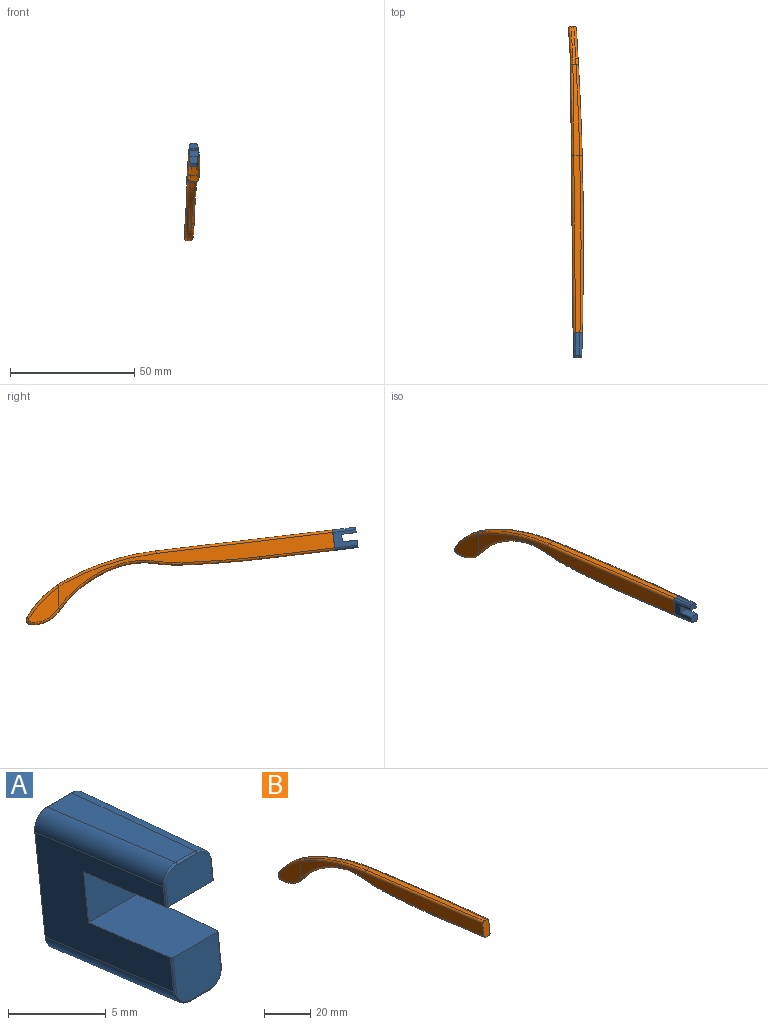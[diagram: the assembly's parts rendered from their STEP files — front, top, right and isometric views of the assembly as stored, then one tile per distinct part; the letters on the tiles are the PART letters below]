
ASSEMBLY  parts=2 mates=1
PART A: 32 faces, bbox 4.2x25.4x61.7 mm
  f0: plane 5.95x3.66mm, normal (0,-0.12,-0.99), area 21.2mm2, adj f1,f3,f11,f12,f27,f31
  f1: plane 3.66x3mm, normal (0,-0.99,0.12), area 11mm2, adj f0,f2,f11,f12
  f2: plane 5.95x3.65mm, normal (0,0.12,0.99), area 21.1mm2, adj f1,f4,f11,f12,f22,f26
  f3: plane 3.23x2.06mm, normal (0,-0.99,0.12), area 6.3mm2, adj f0,f27,f28,f29,f30,f31
  f4: plane 3.34x3.07mm, normal (0,-0.99,0.12), area 9.1mm2, adj f2,f22,f23,f24,f25,f26
  f5: bspline ~23.07x3.72mm, area 14.6mm2, adj f7,f12,f19,f28
  f6: cylinder r=1mm len=9.32mm, axis (0.01,-0.99,0.12), area 14.5mm2, adj f7,f11,f15,f30
  f7: plane 9.18x1.79mm, normal (0,0.12,0.99), area 14.9mm2, adj f5,f6,f17,f29
  f8: cylinder r=1mm len=9.3mm, axis (-0.01,0.99,-0.12), area 14.5mm2, adj f10,f11,f16,f25
  f9: bspline ~16.36x2.92mm, area 14.5mm2, adj f10,f12,f20,f23
  f10: plane 9.18x1.76mm, normal (0,-0.12,-0.99), area 14.6mm2, adj f8,f9,f18,f24
  f11: plane 9.92x7.3mm, normal (-1,-0.01,0), area 40mm2, adj f0,f1,f2,f6,f8,f14,f26,f31
  f12: cylinder r=1319.56mm len=9.92mm, axis (0,0,-1), area 40.1mm2, adj f0,f1,f2,f5,f9,f21,f22,f27
  f13: plane 8.14x3.73mm, normal (0,0.99,-0.12), area 29.6mm2, adj f14,f15,f16,f17,f18,f19,f20,f21
  f14: cylinder r=0.03mm len=6.21mm, axis (0,-0.12,-0.99), area 0.3mm2, adj f11,f13,f15,f16
  f15: bspline ~1.17x1.17mm, area 0.1mm2, adj f6,f13,f14,f17
  f16: bspline ~1x0.99mm, area 0.1mm2, adj f8,f13,f14,f18
  f17: cylinder r=0.03mm len=1.79mm, axis (-1,0,0), area 0.1mm2, adj f7,f13,f15,f19
  f18: cylinder r=0.03mm len=1.76mm, axis (1,0,0), area 0.1mm2, adj f10,f13,f16,f20
  f19: bspline ~1.22x1.22mm, area 0.1mm2, adj f5,f13,f17,f21
  f20: bspline ~1.22x1.22mm, area 0.1mm2, adj f9,f13,f18,f21
  f21: bspline ~31.05x3.72mm, area 0.3mm2, adj f12,f13,f19,f20
  f22: bspline ~36.24x4.4mm, area 0.3mm2, adj f2,f4,f12,f23
  f23: bspline ~1.22x1.22mm, area 0.2mm2, adj f4,f9,f22,f24
  f24: cylinder r=0.1mm len=1.4mm, axis (-1,0,0), area 0.2mm2, adj f4,f10,f23,f25
  f25: bspline ~1.05x1mm, area 0.2mm2, adj f4,f8,f24,f26
  f26: cylinder r=0.1mm len=2.05mm, axis (0,-0.12,-0.99), area 0.3mm2, adj f2,f4,f11,f25
  f27: bspline ~37.57x4.56mm, area 0.2mm2, adj f0,f3,f12,f28
  f28: bspline ~1.22x1.06mm, area 0.2mm2, adj f3,f5,f27,f29
  f29: cylinder r=0.1mm len=1.43mm, axis (-1,0,0), area 0.2mm2, adj f3,f7,f28,f30
  f30: bspline ~1.18x1.04mm, area 0.2mm2, adj f3,f6,f29,f31
  f31: cylinder r=0.1mm len=1.18mm, axis (0,-0.12,-0.99), area 0.2mm2, adj f0,f3,f11,f30
PART B: 49 faces, bbox 7x133.4x39.5 mm
  f0: cylinder r=1319.56mm len=110.95mm, axis (0,0,-1), area 526.6mm2, adj f4,f5,f16,f19,f20,f28,f38,f39
  f1: plane 111.11x30.19mm, normal (-1,-0.01,0), area 527.2mm2, adj f6,f7,f17,f21,f25,f31,f32,f33
  f2: plane 30.17x3.59mm, normal (0,-0.12,-0.99), area 66.7mm2, adj f5,f7,f29,f36
  f3: plane 71.19x8.46mm, normal (0,0.12,0.99), area 173.4mm2, adj f4,f6,f15,f24
  f4: bspline ~96.82x12.47mm, area 112.6mm2, adj f0,f3,f20,f26
  f5: bspline ~55.64x7.58mm, area 47.7mm2, adj f0,f2,f30,f37
  f6: cylinder r=1mm len=71.31mm, axis (0.01,-0.99,0.12), area 112.7mm2, adj f1,f3,f21,f23
  f7: cylinder r=1mm len=30.27mm, axis (-0.01,0.99,-0.12), area 47.7mm2, adj f1,f2,f27,f35
  f8: cylinder r=411.75mm len=31.41mm, axis (-1,0,0), area 79.8mm2, adj f9,f34,f36,f38
  f9: cylinder r=61.54mm len=10.94mm, axis (-1,0,0), area 27.2mm2, adj f8,f10,f33,f39
  f10: cylinder r=31.85mm len=14.47mm, axis (-1,0,0), area 32.5mm2, adj f9,f11,f32,f40
  f11: cylinder r=47.8mm len=24.18mm, axis (-1,0,0), area 47.5mm2, adj f10,f12,f31,f41,f42
  f12: cylinder r=12.7mm len=11.64mm, axis (-1,0,0), area 15.4mm2, adj f11,f13,f31,f43,f45
  f13: cylinder r=1.93mm len=2.91mm, axis (-1,0,0), area 4.6mm2, adj f12,f14,f44,f46
  f14: cylinder r=40.98mm len=15.15mm, axis (-1,0,0), area 24.7mm2, adj f13,f15,f18,f19,f47,f48
  f15: cylinder r=99.37mm len=36.91mm, axis (-1,0,0), area 71.1mm2, adj f3,f14,f20,f21
  f16: plane 14.87x12.97mm, normal (1,0.06,0), area 90.1mm2, adj f0,f18,f41,f42,f43,f44
  f17: plane 14.96x12.98mm, normal (-1,-0.06,0), area 88mm2, adj f1,f45,f46,f48
  f18: bspline ~13.75x13.15mm, area 28mm2, adj f14,f16,f19,f44
  f19: bspline ~8.42x5.33mm, area 4.5mm2, adj f0,f14,f18,f20
  f20: bspline ~37x12.89mm, area 60.7mm2, adj f0,f4,f15,f19
  f21: bspline ~47.28x15.18mm, area 61.3mm2, adj f1,f6,f15,f47
  f22: plane 8.14x3.73mm, normal (0,-0.99,0.12), area 29.6mm2, adj f23,f24,f25,f26,f27,f28,f29,f30
  f23: bspline ~1.17x1.17mm, area 0.1mm2, adj f6,f22,f24,f25
  f24: cylinder r=0.03mm len=1.79mm, axis (1,0,0), area 0.1mm2, adj f3,f22,f23,f26
  f25: cylinder r=0.03mm len=6.21mm, axis (0,0.12,0.99), area 0.3mm2, adj f1,f22,f23,f27
  f26: bspline ~1.22x1.06mm, area 0.1mm2, adj f4,f22,f24,f28
  f27: bspline ~1x1mm, area 0.1mm2, adj f7,f22,f25,f29
  f28: bspline ~6.21x0.77mm, area 0.3mm2, adj f0,f22,f26,f30
  f29: cylinder r=0.03mm len=1.76mm, axis (-1,0,0), area 0.1mm2, adj f2,f22,f27,f30
  f30: bspline ~1.22x1.05mm, area 0.1mm2, adj f5,f22,f28,f29
  f31: bspline ~24.99x18.91mm, area 47.3mm2, adj f1,f11,f12,f32,f45
  f32: bspline ~14.92x2.6mm, area 23.3mm2, adj f1,f10,f31,f33
  f33: bspline ~10.94x1.61mm, area 17.1mm2, adj f1,f9,f32,f34
  f34: bspline ~31.43x3.34mm, area 49.4mm2, adj f1,f8,f33,f35
  f35: sphere r=1mm, area 0mm2, adj f7,f34,f36
  f36: cylinder r=1mm len=2.51mm, axis (-1,0,0), area 0mm2, adj f2,f8,f35,f37
  f37: sphere r=1mm, area 0mm2, adj f5,f36,f38
  f38: bspline ~68.58x5.71mm, area 49.5mm2, adj f0,f8,f37,f39
  f39: bspline ~14.44x1.88mm, area 17.1mm2, adj f0,f9,f38,f40
  f40: bspline ~22.02x3.93mm, area 23.4mm2, adj f0,f10,f39,f41
  f41: bspline ~31.19x21.74mm, area 46.8mm2, adj f0,f11,f16,f40,f42
  f42: bspline ~1.91x1.83mm, area 2.6mm2, adj f11,f16,f41,f43
  f43: bspline ~13.54x7.29mm, area 20.7mm2, adj f12,f16,f42,f44
  f44: bspline ~3.22x1.79mm, area 4.8mm2, adj f13,f16,f18,f43
  f45: bspline ~14.16x8.7mm, area 21.1mm2, adj f1,f12,f17,f31,f46
  f46: bspline ~3.22x1.91mm, area 5.1mm2, adj f13,f17,f45,f48
  f47: bspline ~12.69x7.89mm, area 5mm2, adj f1,f14,f21,f48
  f48: bspline ~17.97x17.93mm, area 29.1mm2, adj f1,f14,f17,f46,f47
PLACE A t=(59.6,-275.25,3.22)mm
PLACE B t=(59.6,-275.27,3.22)mm
MATE fastened B.f22 <-> A.f13  axis (0,-0.99,0.12) through (64.56,-214.98,-10.79)mm
